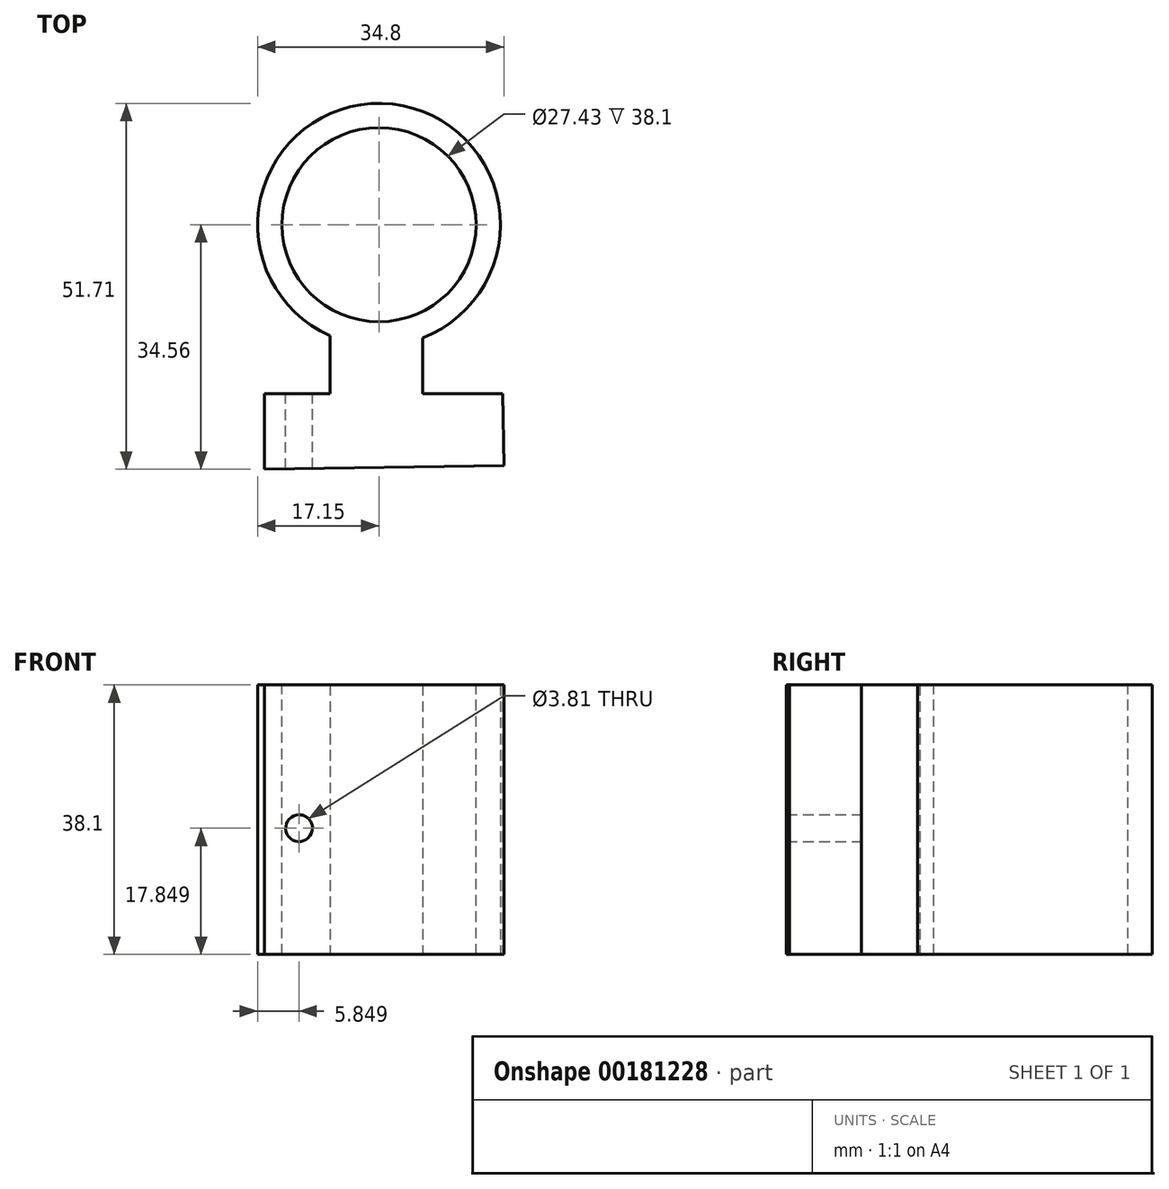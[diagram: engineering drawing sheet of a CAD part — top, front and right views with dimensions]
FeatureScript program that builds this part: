
annotation { "Feature Type Name" : "Feature", "Feature Type Description" : "" }
export const myFeature = defineFeature(function(context is Context, id is Id, definition is map)
    precondition{}
    {
        {
            var Q0;
            Q0=qCreatedBy(makeId("Top.planeOp"),FACE);
            var sketch = newSketch(context, id + "F0", { "sketchPlane" : qUnion([Q0])});
            skCircle(sketch, "E0", {"center": v(0, 0) * mm, "radius": 17.15 * mm});
            skLineSegment(sketch, "E1", {"start": v(6.18, -16) * mm, "end": v(6.18, -21.57) * mm});
            skLineSegment(sketch, "E2", {"start": v(6.18, -21.57) * mm, "end": v(6.18, -23.9) * mm});
            skLineSegment(sketch, "E3", {"start": v(6.18, -23.9) * mm, "end": v(17.5, -23.9) * mm});
            skLineSegment(sketch, "E4", {"start": v(17.5, -23.9) * mm, "end": v(17.65, -34.06) * mm});
            skLineSegment(sketch, "E5", {"start": v(17.65, -34.06) * mm, "end": v(-16.17, -34.56) * mm});
            skLineSegment(sketch, "E6", {"start": v(-16.17, -23.9) * mm, "end": v(-16.17, -34.56) * mm});
            skLineSegment(sketch, "E7", {"start": v(-6.92, -23.9) * mm, "end": v(-16.17, -23.9) * mm});
            skLineSegment(sketch, "E8", {"start": v(-6.92, -15.69) * mm, "end": v(-6.92, -23.9) * mm});
            skSolve(sketch);
        }
        {
            var Q0;
            Q0 = qSketchRegion(id + "F0", true);
            var Q1;
            Q1 = qSketchRegion(id + "F2", true);
            extrude(context, id + "F1", {"entities" : qUnion([Q0, Q1]), "depth" : 38.1 * mm});
        }
        {
            var Q0;
            Q0=makeQuery(id+"F1.opExtrude","CAP_FACE",FACE,{"disambiguationData":[OSD([sQuery(id+"F0.wireOp",EDGE,"E0")])],"isStart":false});
            var sketch = newSketch(context, id + "F2", { "sketchPlane" : qUnion([Q0])});
            skCircle(sketch, "E9", {"center": v(0, 0) * mm, "radius": 13.72 * mm});
            skSolve(sketch);
        }
        {
            var Q0;
            Q0 = qSketchRegion(id + "F2", true);
            extrude(context, id + "F3", {"entities" : qUnion([Q0]), "operationType" : NewBodyOperationType.REMOVE, "oppositeDirection" : true, "depth" : 50.3 * mm});
        }
        {
            var Q0;
            Q0=makeQuery(id+"F1.opExtrude","SWEPT_FACE",FACE,{"disambiguationData":[OSD([sQuery(id+"F0.wireOp",EDGE,"E7")])]});
            var sketch = newSketch(context, id + "F4", { "sketchPlane" : qUnion([Q0])});
            skCircle(sketch, "E10", {"center": v(11.3, 17.85) * mm, "radius": 1.9 * mm});
            skSolve(sketch);
        }
        {
            var Q0;
            Q0 = qSketchRegion(id + "F4", true);
            extrude(context, id + "F5", {"entities" : qUnion([Q0]), "operationType" : NewBodyOperationType.REMOVE, "oppositeDirection" : true, "depth" : 25.4 * mm});
        }
    });
